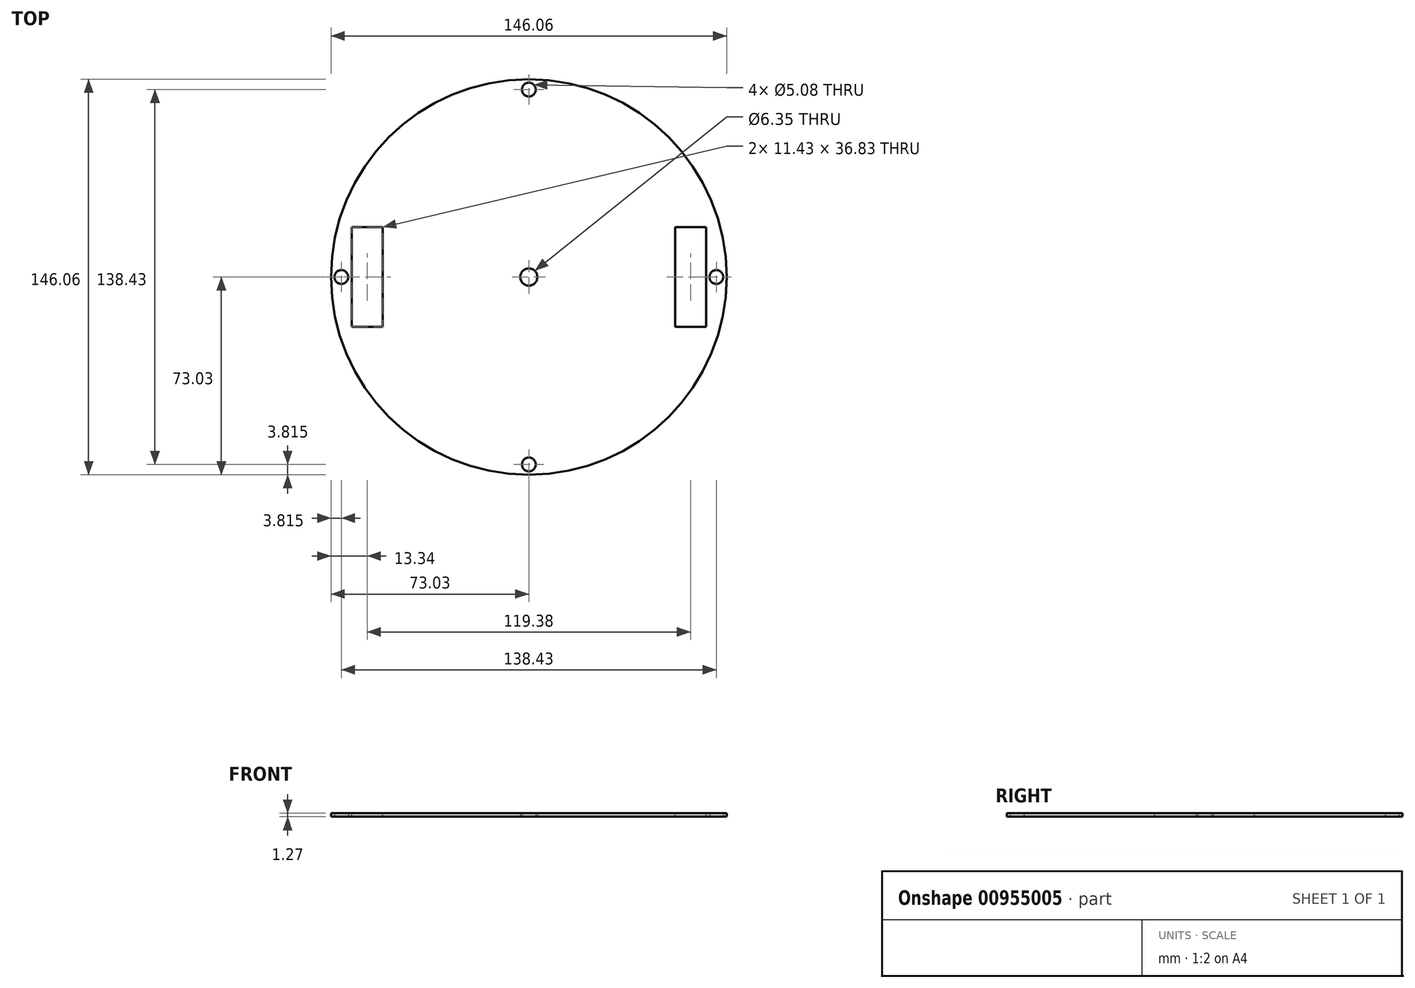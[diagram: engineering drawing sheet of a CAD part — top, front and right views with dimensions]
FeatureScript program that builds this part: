
annotation { "Feature Type Name" : "Feature", "Feature Type Description" : "" }
export const myFeature = defineFeature(function(context is Context, id is Id, definition is map)
    precondition{}
    {
        {
            var Q0;
            Q0=qCreatedBy(makeId("Top.planeOp"),FACE);
            var sketch = newSketch(context, id + "F0", { "sketchPlane" : qUnion([Q0])});
            skCircle(sketch, "E0", {"center": v(0, 0) * mm, "radius": 73.03 * mm});
            skCircle(sketch, "E1", {"center": v(0, 0) * mm, "radius": 69.22 * mm, "construction": true});
            skCircle(sketch, "E2", {"center": v(69.22, 0) * mm, "radius": 2.54 * mm});
            skCircle(sketch, "E3.1.0", {"center": v(0, 69.22) * mm, "radius": 2.54 * mm});
            skCircle(sketch, "E3.2.0", {"center": v(-69.22, 0) * mm, "radius": 2.54 * mm});
            skCircle(sketch, "E3.3.0", {"center": v(0, -69.22) * mm, "radius": 2.54 * mm});
            skCircle(sketch, "E4", {"center": v(0, 0) * mm, "radius": 3.18 * mm});
            skSolve(sketch);
        }
        {
            var Q0;
            Q0=makeQuery(id+"F0.imprint","IMPRINT",FACE,{"disambiguationData":[TD([[makeQuery(id+"F0.imprint","IMPRINT",EDGE,{"derivedFrom":sQuery(id+"F0.wireOp",EDGE,"E0")}),1.0]])]});
            extrude(context, id + "F1", {"entities" : qUnion([Q0]), "depth" : 1.27 * mm, "offsetDistance" : 25.4 * mm});
        }
        {
            var Q0;
            Q0=makeQuery(id+"F1.opExtrude","CAP_FACE",FACE,{"disambiguationData":[OSD([sQuery(id+"F0.wireOp",EDGE,"E0"),sQuery(id+"F0.wireOp",EDGE,"E2"),sQuery(id+"F0.wireOp",EDGE,"E3.1.0"),sQuery(id+"F0.wireOp",EDGE,"E3.2.0"),sQuery(id+"F0.wireOp",EDGE,"E3.3.0")])],"isStart":false});
            var sketch = newSketch(context, id + "F2", { "sketchPlane" : qUnion([Q0])});
            skLineSegment(sketch, "E5.0", {"start": v(-65.4, 18.41) * mm, "end": v(-53.98, 18.41) * mm});
            skLineSegment(sketch, "E5.1", {"start": v(-65.4, -18.41) * mm, "end": v(-65.4, 18.41) * mm});
            skLineSegment(sketch, "E5.2", {"start": v(-53.98, -18.41) * mm, "end": v(-53.98, 18.41) * mm});
            skLineSegment(sketch, "E5.3", {"start": v(-65.4, -18.41) * mm, "end": v(-53.98, -18.41) * mm});
            skLineSegment(sketch, "E5.4", {"start": v(65.4, -18.41) * mm, "end": v(53.98, -18.41) * mm});
            skLineSegment(sketch, "E5.5", {"start": v(53.98, -18.41) * mm, "end": v(53.98, 18.41) * mm});
            skLineSegment(sketch, "E5.6", {"start": v(65.4, -18.41) * mm, "end": v(65.4, 18.41) * mm});
            skLineSegment(sketch, "E5.7", {"start": v(65.4, 18.41) * mm, "end": v(53.98, 18.41) * mm});
            skSolve(sketch);
        }
        {
            var Q0;
            Q0 = qSketchRegion(id + "F2", true);
            extrude(context, id + "F3", {"entities" : qUnion([Q0]), "operationType" : NewBodyOperationType.REMOVE, "endBound" : BoundingType.THROUGH_ALL, "oppositeDirection" : true, "depth" : 25.4 * mm, "offsetDistance" : 25.4 * mm});
        }
    });
